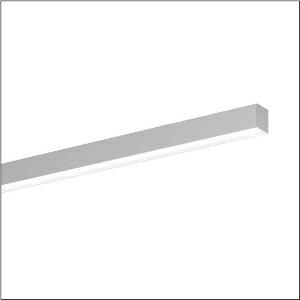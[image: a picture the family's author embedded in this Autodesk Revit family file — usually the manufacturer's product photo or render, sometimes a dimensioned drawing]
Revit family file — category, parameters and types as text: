
# Revit family: silica_r__21_51mx23tctas_d824
name_source: partatom
category: Lighting Fixtures
units: mm (PartAtom-declared; Revit-internal decimal feet)

## family parameters
Cut with Voids When Loaded = No
Host = Face
Light Source = No
Part Type = Normal
Room Calculation Point = No
Round Connector Dimension = Use Diameter
Shared = No

## types (1)
- --- (1 x LED, 8070 lm, 81.1 W, 6500K)
    Apparent Load = 81 VA
    CIE Flux Codes = 78 96 99 100 100
    Color Rendering = 80
    Color Temperature = 6500K
    Default Elevation = 1800 mm
    Description = Silica® 21, office luminaire, primary optical cover: prismatic diffuser, of PMMA, CAT 2 (L<= 3000cd/m²), light emission: direct distribution, primary light characteristic: symmetric, installation type: surface-mounted, LED, rated luminous flux: 8.070lm, luminous efficacy: 95lm/W, light colour: 8tw, colour temperature: 2700..6500K, control gear: ECG DALI, with terminal, 3+2-pole, max. 2.5mm², mains connection: 220..240V, AC, 50/60Hz, rated input power: 85.1W, luminaire housing, of aluminium, metallic grey (RAL 9006), length: 3.004mm, width: 53mm, height: 53mm, protection rating (complete): IP20, insulation class (complete): insulation class I (protective earthing), certification: CE, permissible operating ambient temperature: 0..+35°C, standard: EN 50419, packaging unit: 1 piece
    Height = 0 mm  [stored 0 ft]
    Lamp = 1 x LED
    Lamp Light Flux = 8070 lm
    Lamp Power = 81.1 W
    Lamp count = 1
    Length = 3004 mm
    Luminous efficacy = 100 lm/W
    Manufacturer = Siteco
    ModVariant = No
    Model = 51MX23TCTAS
    Mounting Place = Ceiling
    Mounting Type = Recessed
    Number of Poles = 1
    OnlyDefault = Yes
    Power Factor = 1
    Product Name = Silica® 21
    Product group = office luminaire | ceiling recessed
    ProductGroupID = 401
    Protection Class = Protection class I
    Protection Degree = IP 20
    RLX_Detail_Level = 1
    RLX_Emergency_Light_Flux = 0 lm
    RLX_Emergency_Type = 0
    RLX_Emergency_Type_DB = No
    RlxData = <blob elided: 17921 chars, md5=7030d590>
    Socket = socket
    Standby Power = 0 W
    System Light Flux = 8070 lm
    System Power = 81 W
    Type Comments = individual setting
    Type Image = l_1297768.jpg
    URL = http://relux.com
    VarID = @adj_071113
    Voltage = 0 V
    Weight = 0.00 kg
    Width = 53 mm

note: [stored X ft] marks values corroborated as IEEE doubles in the binary element streams (Revit-internal decimal feet)

## geometry (parser evidence)
native form markers: Blend x4, Sweep x10
no freeform markers — native parametric forms only
